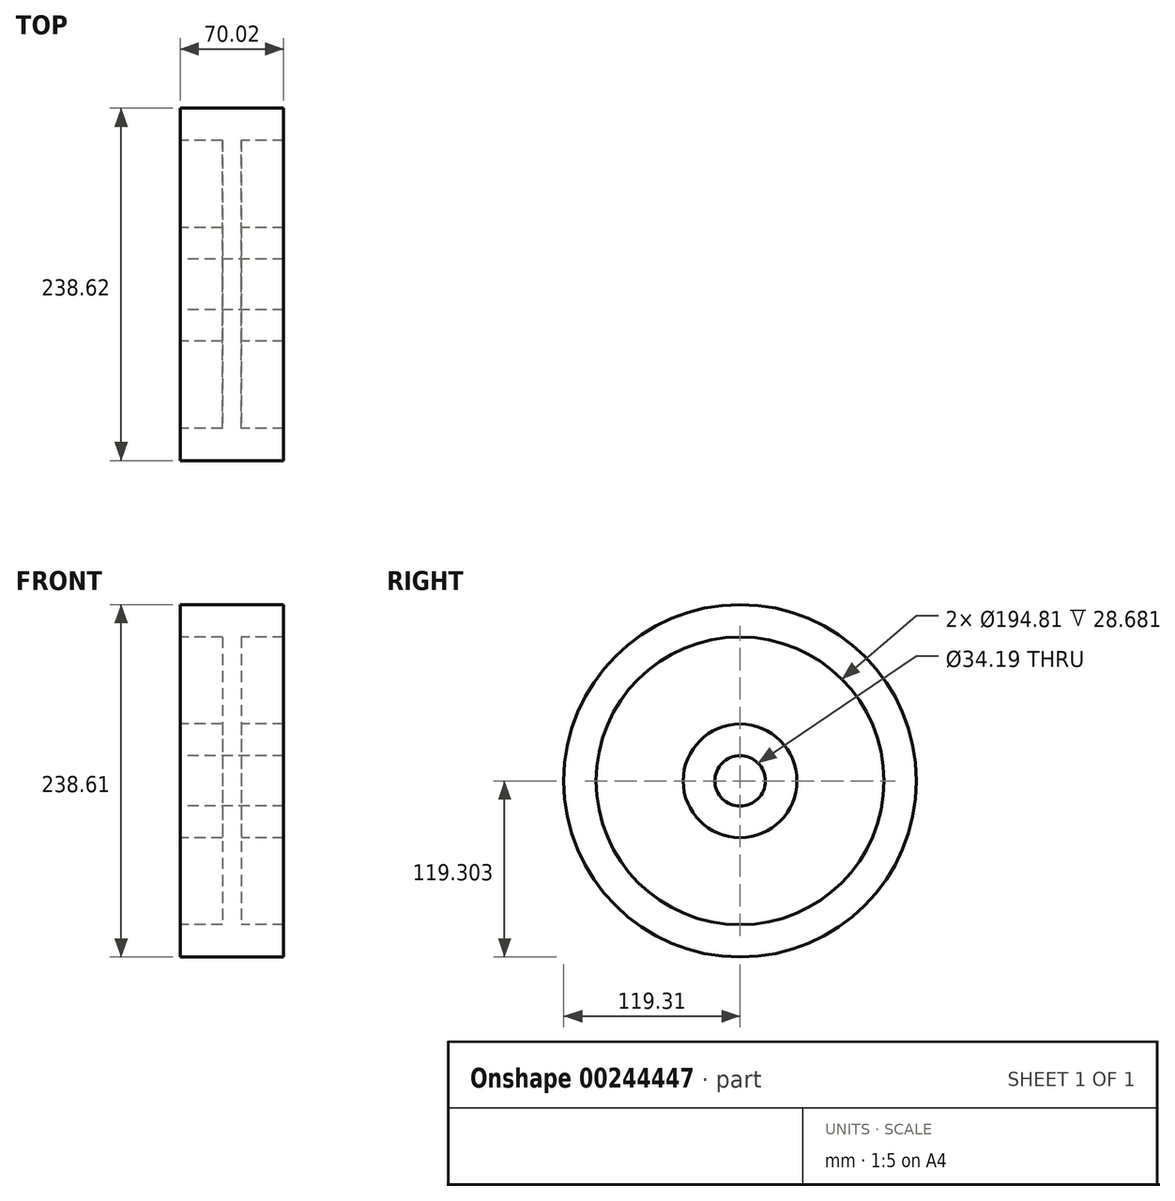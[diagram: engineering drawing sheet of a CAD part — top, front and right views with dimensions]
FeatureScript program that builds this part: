
annotation { "Feature Type Name" : "Feature", "Feature Type Description" : "" }
export const myFeature = defineFeature(function(context is Context, id is Id, definition is map)
    precondition{}
    {
        {
            var Q0;
            Q0=qCreatedBy(makeId("Front.planeOp"),FACE);
            var sketch = newSketch(context, id + "F0", { "sketchPlane" : qUnion([Q0])});
            skLineSegment(sketch, "E0", {"start": v(-35.01, 56.58) * mm, "end": v(35.01, 56.58) * mm});
            skLineSegment(sketch, "E1", {"start": v(35.01, 56.58) * mm, "end": v(35.01, 34.68) * mm});
            skLineSegment(sketch, "E2", {"start": v(35.01, 34.68) * mm, "end": v(6.33, 34.68) * mm});
            skLineSegment(sketch, "E3", {"start": v(6.33, 34.68) * mm, "end": v(6.33, -24.25) * mm});
            skLineSegment(sketch, "E4", {"start": v(6.33, -24.25) * mm, "end": v(35.01, -24.25) * mm});
            skLineSegment(sketch, "E5", {"start": v(35.01, -24.25) * mm, "end": v(35.01, -45.63) * mm});
            skLineSegment(sketch, "E6", {"start": v(35.01, -45.63) * mm, "end": v(-35.01, -45.63) * mm});
            skLineSegment(sketch, "E7", {"start": v(-35.01, -45.63) * mm, "end": v(-35.01, -24.25) * mm});
            skLineSegment(sketch, "E8", {"start": v(-35.01, -24.25) * mm, "end": v(-6.33, -24.25) * mm});
            skLineSegment(sketch, "E9", {"start": v(-6.33, -24.25) * mm, "end": v(-6.33, 34.68) * mm});
            skLineSegment(sketch, "E10", {"start": v(-6.33, 34.68) * mm, "end": v(-35.01, 34.68) * mm});
            skLineSegment(sketch, "E11", {"start": v(-35.01, 56.58) * mm, "end": v(-35.01, 34.68) * mm});
            skLineSegment(sketch, "E12", {"start": v(-94.76, -62.73) * mm, "end": v(109.96, -62.73) * mm, "construction": true});
            skLineSegment(sketch, "E13", {"start": v(0, -62.73) * mm, "end": v(0, 71.37) * mm, "construction": true});
            skSolve(sketch);
        }
        {
            var Q0;
            Q0 = qSketchRegion(id + "F0", true);
            var Q1;
            Q1=sQuery(id+"F0.wireOp",EDGE,"E12");
            revolve(context, id + "F1", {"entities" : qUnion([Q0]), "axis" : qUnion([Q1]), "revolveType" : RevolveType.FULL});
        }
    });
